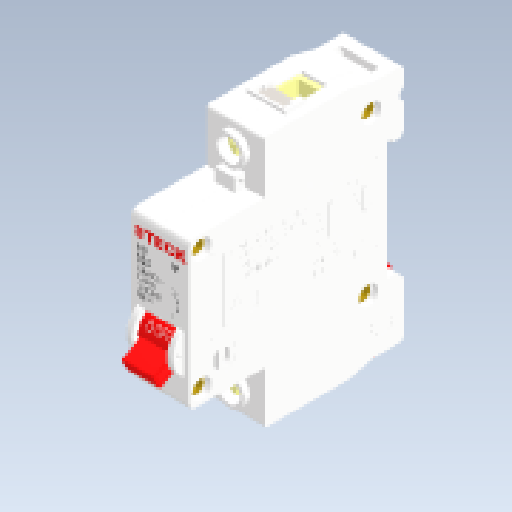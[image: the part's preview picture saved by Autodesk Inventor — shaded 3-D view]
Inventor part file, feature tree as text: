
AUTODESK INVENTOR PART (.ipt)
format: ipt  version: 2025.2 (Build 292293000, 293)  size: 12,350,464 bytes
history: native  units: mm
features: other x52, sketch x4
ambient origin geometry x8: Origin, YZ Plane, XZ Plane, XY Plane, X Axis, Y Axis, Z Axis, Center Point
bodies: Body1 (feature_tree), Body2 (feature_tree), Body3 (feature_tree), Body4 (feature_tree), Body5 (feature_tree), Body6 (feature_tree), Body7 (feature_tree), Body8 (feature_tree), Body9 (feature_tree), Body10 (feature_tree), Body11 (feature_tree), Body12 (feature_tree), Body13 (feature_tree), Body14 (feature_tree), Body15 (feature_tree), Body16 (feature_tree), Body17 (feature_tree), Body18 (feature_tree), Body19 (feature_tree), Body20 (feature_tree), Body21 (feature_tree), Body22 (feature_tree), Body23 (feature_tree), Body24 (feature_tree), Body25 (feature_tree)
feature tree (56):
  other  "Sólido1"
  other  "Edição direta1"
  other  "Edição direta2"
  other  "Edição direta3"
  other  "Sólido2"
  other  "Sólido3"
  other  "Sólido4"
  other  "Sólido5"
  other  "Sólido6"
  other  "Sólido7"
  other  "Sólido8"
  other  "Sólido9"
  other  "Sólido10"
  other  "Sólido11"
  other  "Sólido12"
  other  "Sólido13"
  other  "Sólido14"
  other  "Sólido15"
  other  "Sólido16"
  other  "Sólido17"
  other  "Sólido18"
  other  "Sólido19"
  other  "Sólido20"
  other  "Sólido21"
  other  "Sólido22"
  other  "Sólido23"
  other  "Sólido24"
  other  "Sólido25"
  other  "Chanfro4"
  other  "Inclinação3"
  other  "Espelhar1[1]"
  other  "Espelhar1[2]"
  other  "Envolver1"
  other  "Filete11"
  other  "Revolução1"
  sketch  "Esboço-padrão1[1]"  dims[d0=4.0mm d1=10.0mm d2=10.0mm]
  sketch  "Esboço-padrão1[2]"  dims[d3=12.0mm d4=10.0mm d5=10.0mm]
  sketch  "Esboço-padrão1[3]"  dims[d6=9.0mm d7=10.0mm d8=10.0mm]
  sketch  "Esboço-padrão1[4]"
  other  "Ressalto-extrusão38"
  other  "Ressalto-extrusão31[2]"
  other  "Ressalto-extrusão31[3]"
  other  "Ressalto-extrusão37[2]"
  other  "Ressalto-extrusão37[3]"
  other  "Ressalto-extrusão37[4]"
  other  "Ressalto-extrusão37[5]"
  other  "Dividir1[1]"
  other  "Dividir1[2]"
  other  "Dividir1[3]"
  other  "Dividir1[4]"
  other  "Dividir1[5]"
  other  "Dividir1[6]"
  other  "Dividir1[7]"
  other  "Escala1"
  other  "Escala2"
  other  "Escala3"
